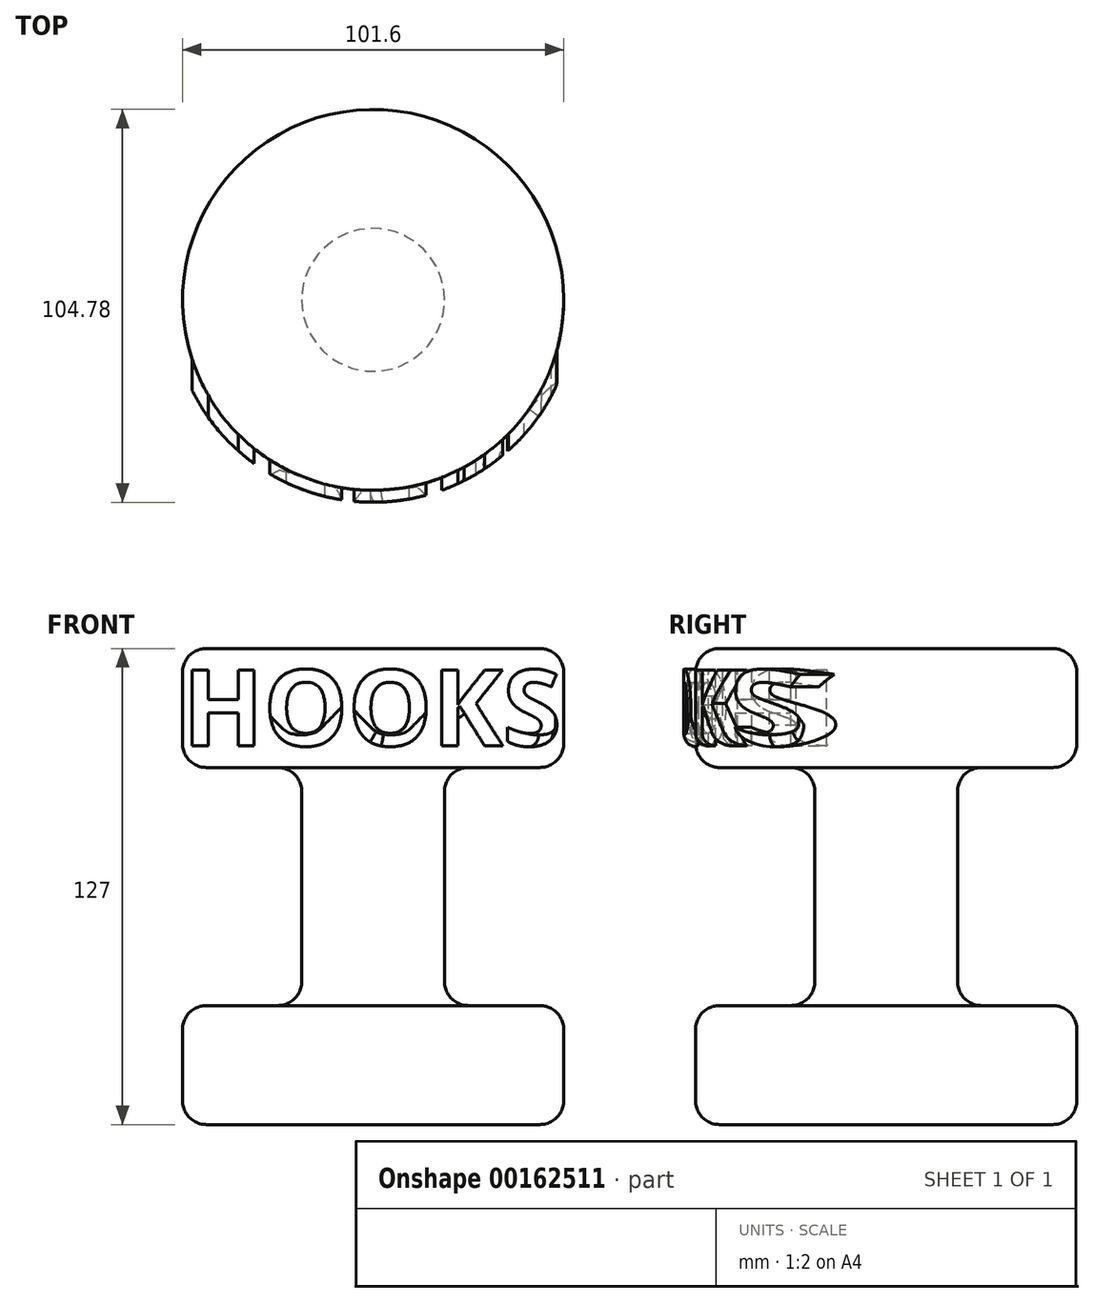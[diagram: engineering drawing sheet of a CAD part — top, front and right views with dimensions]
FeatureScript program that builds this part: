
annotation { "Feature Type Name" : "Feature", "Feature Type Description" : "" }
export const myFeature = defineFeature(function(context is Context, id is Id, definition is map)
    precondition{}
    {
        {
            var Q0;
            Q0=qCreatedBy(makeId("Front.planeOp"),FACE);
            var sketch = newSketch(context, id + "F0", { "sketchPlane" : qUnion([Q0])});
            skLineSegment(sketch, "E0", {"start": v(0, 63.5) * mm, "end": v(0, -63.5) * mm});
            skLineSegment(sketch, "E1", {"start": v(0, -63.5) * mm, "end": v(-44.45, -63.5) * mm});
            skLineSegment(sketch, "E2", {"start": v(-50.8, -57.15) * mm, "end": v(-50.8, -38.1) * mm});
            skLineSegment(sketch, "E3", {"start": v(-44.45, -31.75) * mm, "end": v(-25.4, -31.75) * mm});
            skLineSegment(sketch, "E4", {"start": v(-19.05, -25.4) * mm, "end": v(-19.05, 25.4) * mm});
            skLineSegment(sketch, "E5", {"start": v(-25.4, 31.75) * mm, "end": v(-44.45, 31.75) * mm});
            skLineSegment(sketch, "E6", {"start": v(-50.8, 38.1) * mm, "end": v(-50.8, 57.15) * mm});
            skLineSegment(sketch, "E7", {"start": v(-44.45, 63.5) * mm, "end": v(0, 63.5) * mm});
            skPoint(sketch, "E8.visualSharp", {"position": v(-19.05, -31.75) * mm});
            skArc(sketch, "E8.filletArc", {"start": v(-25.4, -31.75) * mm, "mid": v(-20.9, -29.9) * mm, "end": v(-19.05, -25.4) * mm});
            skPoint(sketch, "E9.visualSharp", {"position": v(-19.05, 31.75) * mm});
            skArc(sketch, "E9.filletArc", {"start": v(-19.05, 25.4) * mm, "mid": v(-20.9, 29.9) * mm, "end": v(-25.4, 31.75) * mm});
            skPoint(sketch, "E10.visualSharp", {"position": v(-50.8, 31.75) * mm});
            skArc(sketch, "E10.filletArc", {"start": v(-50.8, 38.1) * mm, "mid": v(-48.94, 33.6) * mm, "end": v(-44.45, 31.75) * mm});
            skPoint(sketch, "E11.visualSharp", {"position": v(-50.8, 63.5) * mm});
            skArc(sketch, "E11.filletArc", {"start": v(-44.45, 63.5) * mm, "mid": v(-48.94, 61.64) * mm, "end": v(-50.8, 57.15) * mm});
            skPoint(sketch, "E12.visualSharp", {"position": v(-50.8, -31.75) * mm});
            skArc(sketch, "E12.filletArc", {"start": v(-44.45, -31.75) * mm, "mid": v(-48.94, -33.6) * mm, "end": v(-50.8, -38.1) * mm});
            skPoint(sketch, "E13.visualSharp", {"position": v(-50.8, -63.5) * mm});
            skArc(sketch, "E13.filletArc", {"start": v(-50.8, -57.15) * mm, "mid": v(-48.94, -61.64) * mm, "end": v(-44.45, -63.5) * mm});
            skLineSegment(sketch, "E14", {"start": v(0, 0) * mm, "end": v(-19.05, 0) * mm});
            skSolve(sketch);
        }
        {
            var Q0;
            Q0 = qSketchRegion(id + "F0", true);
            var Q1;
            Q1=sQuery(id+"F0.wireOp",EDGE,"E0");
            revolve(context, id + "F1", {"entities" : qUnion([Q0]), "axis" : qUnion([Q1]), "revolveType" : RevolveType.FULL});
        }
        {
            var Q0;
            Q0=qCreatedBy(makeId("Front.planeOp"),FACE);
            var sketch = newSketch(context, id + "F2", { "sketchPlane" : qUnion([Q0])});
            skText(sketch, "E15", { "text": "HOOKS", "fontName": "OpenSans-Bold.ttf"});
            const initialGuessF2  = {"E15": [-0.0508, 0.03756, 1, 0, 0.02034]};
            skSetInitialGuess(sketch, initialGuessF2);
            skSolve(sketch);
        }
        {
            var Q0;
            Q0 = qSketchRegion(id + "F2", true);
            extrude(context, id + "F3", {"entities" : qUnion([Q0]), "operationType" : NewBodyOperationType.ADD, "depth" : 60.45 * mm});
        }
        {
            var Q0;
            Q0=qCreatedBy(makeId("Right.planeOp"),FACE);
            var sketch = newSketch(context, id + "F4", { "sketchPlane" : qUnion([Q0])});
            skLineSegment(sketch, "E16.bottom", {"start": v(124.83, 73.14) * mm, "end": v(53.98, 73.14) * mm});
            skLineSegment(sketch, "E16.top", {"start": v(124.83, 19.33) * mm, "end": v(53.98, 19.33) * mm});
            skLineSegment(sketch, "E16.left", {"start": v(124.83, 73.14) * mm, "end": v(124.83, 19.33) * mm});
            skLineSegment(sketch, "E16.right", {"start": v(53.97, 73.14) * mm, "end": v(53.97, 19.33) * mm});
            skLineSegment(sketch, "E17", {"start": v(0, 67.4) * mm, "end": v(0, 6.05) * mm});
            skSolve(sketch);
        }
        {
            var Q0;
            Q0=makeQuery(id+"F4.imprint","IMPRINT",FACE,{"disambiguationData":[TD([[makeQuery(id+"F4.imprint","IMPRINT",EDGE,{"derivedFrom":sQuery(id+"F4.wireOp",EDGE,"E16.bottom")}),1.0]])]});
            var Q1;
            Q1=sQuery(id+"F4.wireOp",EDGE,"E17");
            revolve(context, id + "F5", {"operationType" : NewBodyOperationType.REMOVE, "entities" : qUnion([Q0]), "axis" : qUnion([Q1]), "revolveType" : RevolveType.FULL, "oppositeDirection" : true});
        }
        {
            var Q0;
            Q0=makeQuery(id+"F5.boolean.opBoolean","INTERSECT",EDGE,{"derivedFrom":[makeQuery(id+"F3.opExtrude","SWEPT_FACE",FACE,{"disambiguationData":[OSD([sQuery(id+"F2.wireOp",EDGE,"E15.sketch_text.stroke-4")])]}),makeQuery(id+"F5.opRevolve","SWEPT_FACE",FACE,{"disambiguationData":[OSD([sQuery(id+"F4.wireOp",EDGE,"E16.right")])]})]});
            var Q1;
            Q1=makeQuery(id+"F5.boolean.opBoolean","INTERSECT",EDGE,{"derivedFrom":[makeQuery(id+"F3.opExtrude","SWEPT_FACE",FACE,{"disambiguationData":[OSD([sQuery(id+"F2.wireOp",EDGE,"E15.sketch_text.stroke-0")])]}),makeQuery(id+"F5.opRevolve","SWEPT_FACE",FACE,{"disambiguationData":[OSD([sQuery(id+"F4.wireOp",EDGE,"E16.right")])]})]});
            var Q2;
            Q2=makeQuery(id+"F5.boolean.opBoolean","INTERSECT",EDGE,{"derivedFrom":[makeQuery(id+"F3.opExtrude","SWEPT_FACE",FACE,{"disambiguationData":[OSD([sQuery(id+"F2.wireOp",EDGE,"E15.sketch_text.stroke-14")])]}),makeQuery(id+"F5.opRevolve","SWEPT_FACE",FACE,{"disambiguationData":[OSD([sQuery(id+"F4.wireOp",EDGE,"E16.right")])]})]});
            var Q3;
            Q3=makeQuery(id+"F5.boolean.opBoolean","INTERSECT",EDGE,{"derivedFrom":[makeQuery(id+"F3.opExtrude","SWEPT_FACE",FACE,{"disambiguationData":[OSD([sQuery(id+"F2.wireOp",EDGE,"E15.sketch_text.stroke-27")])]}),makeQuery(id+"F5.opRevolve","SWEPT_FACE",FACE,{"disambiguationData":[OSD([sQuery(id+"F4.wireOp",EDGE,"E16.right")])]})]});
            var Q4;
            Q4=makeQuery(id+"F5.boolean.opBoolean","INTERSECT",EDGE,{"derivedFrom":[makeQuery(id+"F3.opExtrude","SWEPT_FACE",FACE,{"disambiguationData":[OSD([sQuery(id+"F2.wireOp",EDGE,"E15.sketch_text.stroke-44")])]}),makeQuery(id+"F5.opRevolve","SWEPT_FACE",FACE,{"disambiguationData":[OSD([sQuery(id+"F4.wireOp",EDGE,"E16.right")])]})]});
            var Q5;
            Q5=makeQuery(id+"F5.boolean.opBoolean","INTERSECT",EDGE,{"derivedFrom":[makeQuery(id+"F3.opExtrude","SWEPT_FACE",FACE,{"disambiguationData":[OSD([sQuery(id+"F2.wireOp",EDGE,"E15.sketch_text.stroke-40")])]}),makeQuery(id+"F5.opRevolve","SWEPT_FACE",FACE,{"disambiguationData":[OSD([sQuery(id+"F4.wireOp",EDGE,"E16.right")])]})]});
            var Q6;
            Q6=makeQuery(id+"F5.boolean.opBoolean","INTERSECT",EDGE,{"derivedFrom":[makeQuery(id+"F3.opExtrude","SWEPT_FACE",FACE,{"disambiguationData":[OSD([sQuery(id+"F2.wireOp",EDGE,"E15.sketch_text.stroke-55")])]}),makeQuery(id+"F5.opRevolve","SWEPT_FACE",FACE,{"disambiguationData":[OSD([sQuery(id+"F4.wireOp",EDGE,"E16.right")])]})]});
            var Q7;
            Q7=makeQuery(id+"F5.boolean.opBoolean","INTERSECT",EDGE,{"derivedFrom":[makeQuery(id+"F3.opExtrude","SWEPT_FACE",FACE,{"disambiguationData":[OSD([sQuery(id+"F2.wireOp",EDGE,"E15.sketch_text.stroke-28")])]}),makeQuery(id+"F5.opRevolve","SWEPT_FACE",FACE,{"disambiguationData":[OSD([sQuery(id+"F4.wireOp",EDGE,"E16.right")])]})]});
            var Q8;
            Q8=makeQuery(id+"F5.boolean.opBoolean","INTERSECT",EDGE,{"derivedFrom":[makeQuery(id+"F3.opExtrude","SWEPT_FACE",FACE,{"disambiguationData":[OSD([sQuery(id+"F2.wireOp",EDGE,"E15.sketch_text.stroke-12")])]}),makeQuery(id+"F5.opRevolve","SWEPT_FACE",FACE,{"disambiguationData":[OSD([sQuery(id+"F4.wireOp",EDGE,"E16.right")])]})]});
            var Q9;
            Q9=makeQuery(id+"F5.boolean.opBoolean","INTERSECT",EDGE,{"derivedFrom":[makeQuery(id+"F3.opExtrude","SWEPT_FACE",FACE,{"disambiguationData":[OSD([sQuery(id+"F2.wireOp",EDGE,"E15.sketch_text.stroke-13")])]}),makeQuery(id+"F5.opRevolve","SWEPT_FACE",FACE,{"disambiguationData":[OSD([sQuery(id+"F4.wireOp",EDGE,"E16.right")])]})]});
            var Q10;
            Q10=makeQuery(id+"F5.boolean.opBoolean","INTERSECT",EDGE,{"derivedFrom":[makeQuery(id+"F3.opExtrude","SWEPT_FACE",FACE,{"disambiguationData":[OSD([sQuery(id+"F2.wireOp",EDGE,"E15.sketch_text.stroke-42")])]}),makeQuery(id+"F5.opRevolve","SWEPT_FACE",FACE,{"disambiguationData":[OSD([sQuery(id+"F4.wireOp",EDGE,"E16.right")])]})]});
            var Q11;
            Q11=makeQuery(id+"F5.boolean.opBoolean","INTERSECT",EDGE,{"derivedFrom":[makeQuery(id+"F3.opExtrude","SWEPT_FACE",FACE,{"disambiguationData":[OSD([sQuery(id+"F2.wireOp",EDGE,"E15.sketch_text.stroke-53")])]}),makeQuery(id+"F5.opRevolve","SWEPT_FACE",FACE,{"disambiguationData":[OSD([sQuery(id+"F4.wireOp",EDGE,"E16.right")])]})]});
            fillet(context, id + "F6", {"entities" : qUnion([Q0, Q1, Q2, Q3, Q4, Q5, Q6, Q7, Q8, Q9, Q10, Q11]), "radius" : 3.17 * mm, "allowEdgeOverflow" : false});
        }
    });
